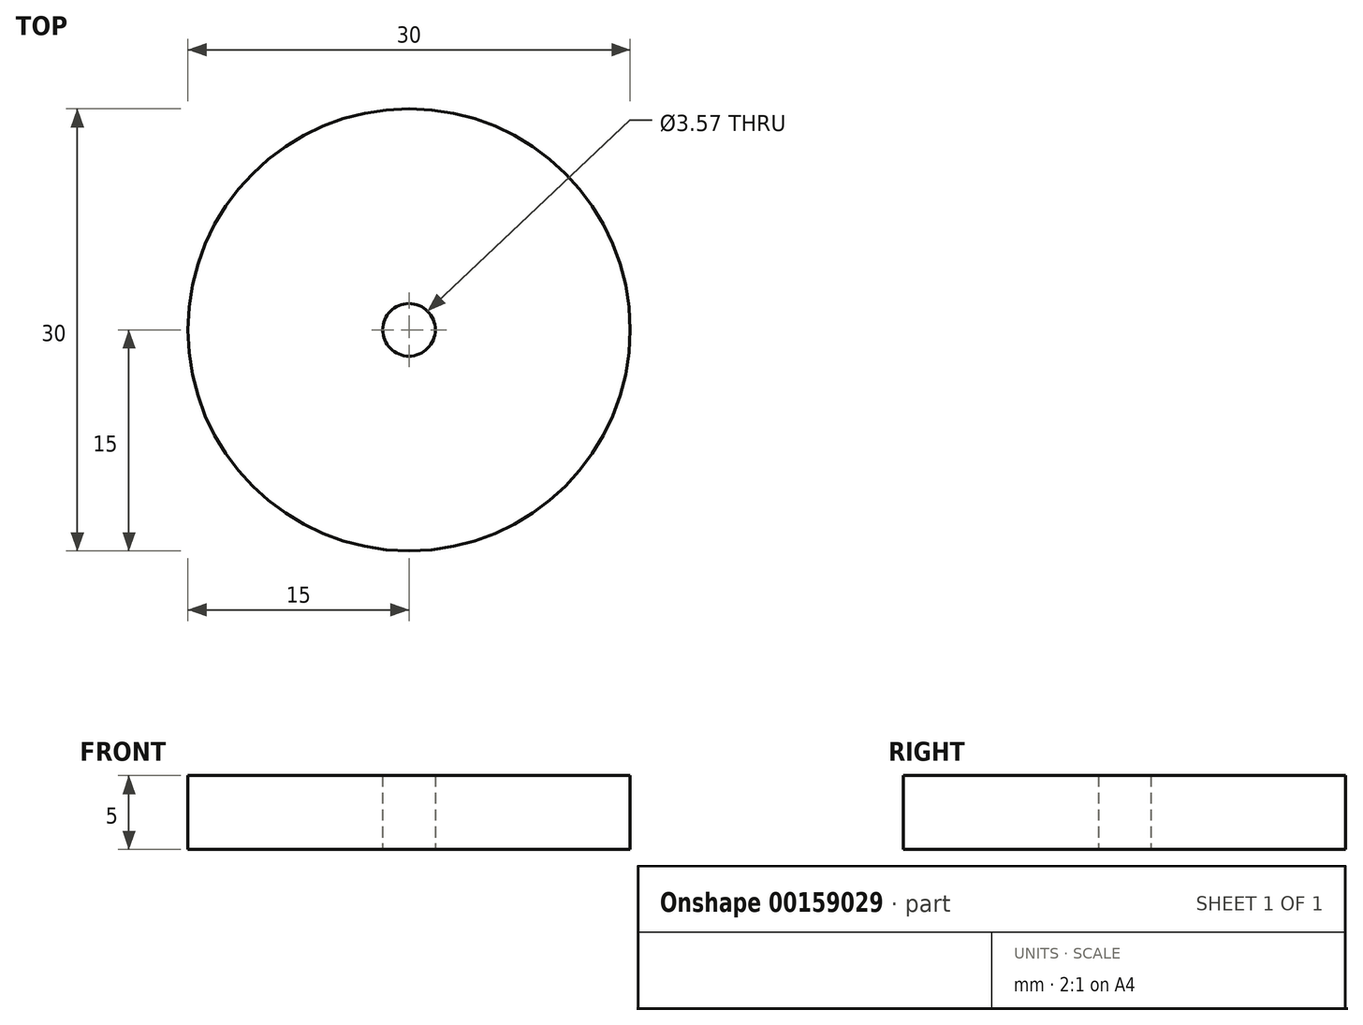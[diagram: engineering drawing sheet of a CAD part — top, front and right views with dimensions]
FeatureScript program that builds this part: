
annotation { "Feature Type Name" : "Feature", "Feature Type Description" : "" }
export const myFeature = defineFeature(function(context is Context, id is Id, definition is map)
    precondition{}
    {
        {
            var Q0;
            Q0=qCreatedBy(makeId("Top.planeOp"),FACE);
            var sketch = newSketch(context, id + "F0", { "sketchPlane" : qUnion([Q0])});
            skCircle(sketch, "E0", {"center": v(0, 0) * mm, "radius": 15 * mm});
            skCircle(sketch, "E1", {"center": v(0, 0) * mm, "radius": 1.79 * mm});
            skSolve(sketch);
        }
        {
            var Q0;
            Q0=makeQuery(id+"F0.imprint","IMPRINT",FACE,{"disambiguationData":[TD([[makeQuery(id+"F0.imprint","IMPRINT",EDGE,{"derivedFrom":sQuery(id+"F0.wireOp",EDGE,"E0")}),1.0]])]});
            extrude(context, id + "F1", {"entities" : qUnion([Q0]), "depth" : 5 * mm});
        }
    });
